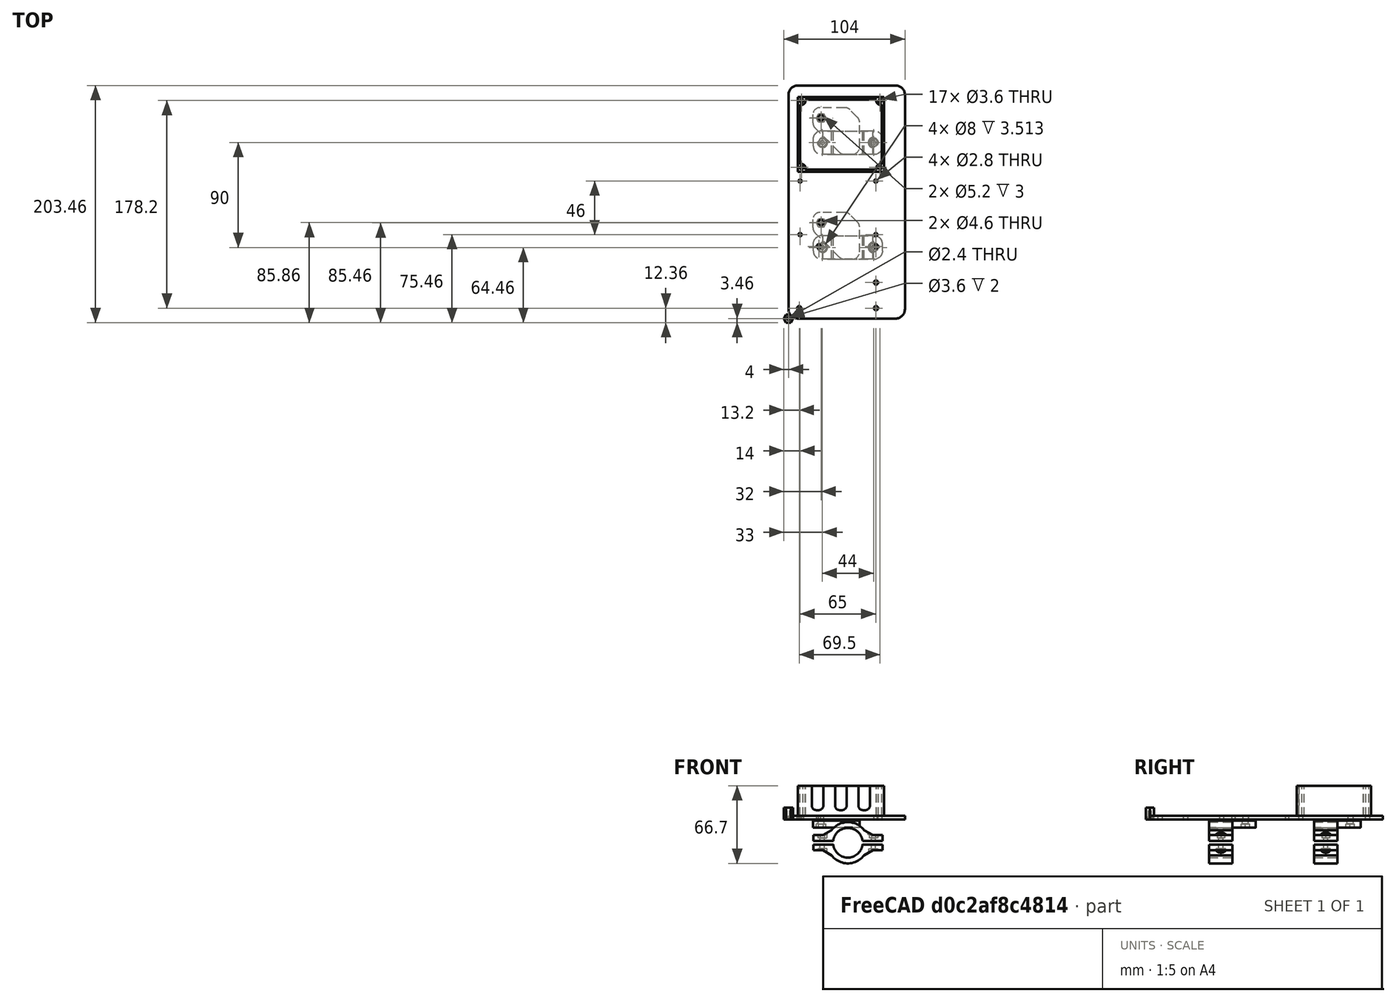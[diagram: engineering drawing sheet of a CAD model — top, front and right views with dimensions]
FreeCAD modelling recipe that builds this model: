
FCSTD DOCUMENT  (FreeCAD 0.18.4R)
Label: cnc_encoders
License: All rights reserved
LicenseURL: http://en.wikipedia.org/wiki/All_rights_reserved
objects: Part::Cylinder×9, PartDesign::FeatureBase×8, PartDesign::Body×8, Part::Cut×7, Part::Box×5, Part::FeaturePython×5, App::Part×3, Part::MultiFuse×2, Part::Fillet×2, Part::Feature×1, Spreadsheet::Sheet×1, Part::Compound×1, Part::RegularPolygon×1, Part::Extrusion×1
note: 50 computed .brp shape members not serialized (recipe doc carries the construction recipe); baked Part::Feature solids carry a one-line shape summary decoded from their .brp

FEATURE [Part::Box] Box  label="base plate"
  AttacherType = Attacher::AttachEngine3D
  Height = 3
  Length = 100
  Width = 200
FEATURE [Part::Cylinder] Cylinder  label="m3 bolt hole"
  Angle = 360
  AttacherType = Attacher::AttachEngine3D
  Height = 10
  Radius = 1.8
FEATURE [PartDesign::FeatureBase] Clone
  BaseFeature = -> Cylinder
FEATURE [PartDesign::Body] Body  label="m3 bolt hole clone"
  BaseFeature = -> Cylinder
  Group = -> [Clone]
  Origin = -> Origin001
  Placement = pos=(-19,27.5,0) rot=(0,0,1;0rad)
  Tip = -> Clone
FEATURE [PartDesign::FeatureBase] Clone001
  BaseFeature = -> Cylinder
FEATURE [PartDesign::Body] Body001  label="m3 bolt hole clone001"
  BaseFeature = -> Cylinder
  Group = -> [Clone001]
  Origin = -> Origin002
  Placement = pos=(-35.8,-25.5,0) rot=(0,0,1;0rad)
  Tip = -> Clone001
FEATURE [PartDesign::FeatureBase] Clone002
  BaseFeature = -> Cylinder
FEATURE [PartDesign::Body] Body002  label="m3 bolt hole clone002"
  BaseFeature = -> Cylinder
  Group = -> [Clone002]
  Origin = -> Origin003
  Placement = pos=(30.2,27.5,0) rot=(0,0,1;0rad)
  Tip = -> Clone002
FEATURE [PartDesign::FeatureBase] Clone003
  BaseFeature = -> Cylinder
FEATURE [PartDesign::Body] Body003  label="m3 bolt hole clone003"
  BaseFeature = -> Cylinder
  Group = -> [Clone003]
  Origin = -> Origin004
  Placement = pos=(30.2,-3.5,0) rot=(0,0,1;0rad)
  Tip = -> Clone003
FEATURE [Part::Feature] cnc_shield_v4_base001
  shape: bbox 75 x 62 x 8 mm, 926 faces, 0 solids (baked)
FEATURE [Part::Box] Box001  label="Cube001"
  AttacherType = Attacher::AttachEngine3D
  Height = 10
  Length = 100
  Placement = pos=(-53,-42,-7) rot=(0,0,1;0rad)
  Width = 100
FEATURE [Part::Cut] Cut  label="test cncv4"
  Base = -> cnc_shield_v4_base001
  Tool = -> Box001
FEATURE [PartDesign::FeatureBase] Clone004
  BaseFeature = -> Cylinder
FEATURE [PartDesign::Body] Body004  label="m3 bolt hole clone004"
  BaseFeature = -> Cylinder
  Group = -> [Clone004]
  Origin = -> Origin005
  Placement = pos=(30.2,-25.5,0) rot=(0,0,1;0rad)
  Tip = -> Clone004
FEATURE [Part::Cylinder] Cylinder001  label="m2.5 bolt hole"
  Angle = 360
  AttacherType = Attacher::AttachEngine3D
  Height = 10
  Radius = 1.4
FEATURE [PartDesign::FeatureBase] Clone005
  BaseFeature = -> Cylinder001
FEATURE [PartDesign::Body] Body005  label="m2.5 bolt hole clone"
  BaseFeature = -> Cylinder001
  Group = -> [Clone005]
  Origin = -> Origin006
  Tip = -> Clone005
FEATURE [Part::FeaturePython] Array  label="m2.5 bolt hole 7x5 pcb array"  # Draft array (typed FeaturePython)
  Angle = 360
  ArrayType = 0
  Axis = (0,0,1)
  Base = -> Body005
  Center = (0,0,0)
  Fuse = false
  IntervalAxis = (0,0,0)
  IntervalX = (65,0,0)
  IntervalY = (0,46,0)
  IntervalZ = (0,0,1)
  NumberPolar = 1
  NumberX = 2
  NumberY = 2
  NumberZ = 1
  Placement = pos=(-35,37.6,0) rot=(0,0,1;0rad)
FEATURE [Part::Cylinder] Cylinder002  label="attach bolt"
  Angle = 360
  AttacherType = Attacher::AttachEngine3D
  Height = 20
  Radius = 2.3
FEATURE [Part::FeaturePython] Array001  label="attach m4 bolt array"  # Draft array (typed FeaturePython)
  Angle = 360
  ArrayType = 0
  Axis = (0,0,1)
  Base = -> Cylinder002
  Center = (0,0,0)
  Fuse = false
  IntervalAxis = (0,0,0)
  IntervalX = (1,0,0)
  IntervalY = (0,90,0)
  IntervalZ = (0,0,1)
  NumberPolar = 1
  NumberX = 1
  NumberY = 2
  NumberZ = 1
  Placement = pos=(-17,48,-6) rot=(0,0,1;0rad)
FEATURE [Spreadsheet::Sheet] Spreadsheet  label="p"
  cells = A1=pcb_length; B1(pcb_length)=70; A2=pcb_width; B2(pcb_width)=50; A3=pcb_hole_x_dist; B3(pcb_hole_x_dist)=65.5; A4=pcb_hole_y_dist; B4(pcb_hole_y_dist)=45.5; A5=bottom_plate_height; B5(bottom_plate_height)=3; A6=bottom_plate_length; B6(bottom_plate_length)=74; A7=bottom_plate_width; B7(bottom_plate_width)=64; A8=bottom_plate_pcb_hole_x_offset; B8(bottom_plate_pcb_hole_x_offset)==(p.bottom_plate_length - p.pcb_hole_x_dist) / 2; A9=bottom_plate_pcb_hole_y_offset; B9(bottom_plate_pcb_hole_y_offset)==(p.bottom_plate_width - p.pcb_hole_y_dist) / 2; A10=box_wall; B10(box_wall)=2; A11=box_wall_height; B11(box_wall_height)=26; A12=box_wall_hole_r; B12(box_wall_hole_r)=1.3; A13=button_hole_r; B13(button_hole_r)=2; A14=tft_hole_length; B14(tft_hole_length)=30; A15=tft_hole_width; B15(tft_hole_width)=14; A16=tft_bolt_hole_dist_x; B16(tft_bolt_hole_dist_x)=25; A17=tft_bolt_hole_dist_y; B17(tft_bolt_hole_dist_y)=19; A19=
FEATURE [Part::Box] Box007  label="wall outer box"
  AttacherType = Attacher::AttachEngine3D
  Height = 26
  Length = 74
  Width = 64
  expr: Height = p.box_wall_height
  expr: Width = p.bottom_plate_width
  expr: Length = p.bottom_plate_length
FEATURE [Part::Box] Box008  label="wall inner extraction"
  AttacherType = Attacher::AttachEngine3D
  Height = 26
  Length = 70
  Placement = pos=(2,2,0) rot=(0,0,1;0rad)
  Width = 60
  expr: Height = p.box_wall_height
  expr: Placement.Base.y = p.box_wall
  expr: Placement.Base.x = p.box_wall
  expr: Width = p.bottom_plate_width - 2 * p.box_wall
  expr: Length = p.bottom_plate_length - 2 * p.box_wall
FEATURE [Part::Cut] Cut004  label="wall box cut"
  Base = -> Box007
  Tool = -> Box008
FEATURE [Part::Cylinder] Cylinder006  label="wall box hole body"
  Angle = 360
  AttacherType = Attacher::AttachEngine3D
  Height = 26
  Radius = 3.3
  expr: Radius = p.box_wall_hole_r + p.box_wall
  expr: Height = p.box_wall_height
FEATURE [Part::Cylinder] Cylinder007  label="wall box hole"
  Angle = 360
  AttacherType = Attacher::AttachEngine3D
  Height = 26
  Radius = 1.3
  expr: Radius = p.box_wall_hole_r
  expr: Height = p.box_wall_height
FEATURE [Part::Cut] Cut005  label="wall box hole stand"
  Base = -> Cylinder006
  Placement = pos=(3.3,3.3,0) rot=(0,0,1;0rad)
  Tool = -> Cylinder007
  expr: Placement.Base.y = p.box_wall + p.box_wall_hole_r
  expr: Placement.Base.x = p.box_wall + p.box_wall_hole_r
FEATURE [Part::FeaturePython] Array004  label="wall box hole stand array"  # Draft array (typed FeaturePython)
  Angle = 360
  ArrayType = 0
  Axis = (0,0,1)
  Base = -> Cut005
  Center = (0,0,0)
  Fuse = false
  IntervalAxis = (0,0,0)
  IntervalX = (67.4,0,0)
  IntervalY = (0,57.4,0)
  IntervalZ = (0,0,1)
  NumberPolar = 1
  NumberX = 2
  NumberY = 2
  NumberZ = 1
  expr: IntervalY.y = p.bottom_plate_width - 2 * (p.box_wall + p.box_wall_hole_r)
  expr: IntervalX.x = p.bottom_plate_length - 2 * (p.box_wall + p.box_wall_hole_r)
FEATURE [Part::MultiFuse] Fusion003  label="wall fusion"
  Placement = pos=(0,0,3) rot=(0,0,1;0rad)
  Shapes = -> [Array004,Cut004]
  expr: Placement.Base.z = p.bottom_plate_height
FEATURE [Part::Box] Box010  label="wall fusion wire hole"
  AttacherType = Attacher::AttachEngine3D
  Height = 21
  Length = 10
  Placement = pos=(34.5,-4.5,8) rot=(0,0,1;0rad)
  Width = 10
  expr: Height = p.box_wall_height - 5
FEATURE [Part::Fillet] Fillet001  label="wall hole fillet"
  Base = -> Box010
  Edges = 2 edges r=4: [Edge4,Edge8]
FEATURE [Part::Cylinder] Cylinder011  label="wall box hole through001"
  Angle = 360
  AttacherType = Attacher::AttachEngine3D
  Height = 20
  Placement = pos=(3.3,3.3,0) rot=(0,0,1;0rad)
  Radius = 1.8
  expr: Placement.Base.y = p.box_wall + p.box_wall_hole_r
  expr: Placement.Base.x = p.box_wall + p.box_wall_hole_r
FEATURE [Part::FeaturePython] Array007  label="wall box hole stand array002"  # Draft array (typed FeaturePython)
  Angle = 360
  ArrayType = 0
  Axis = (0,0,1)
  Base = -> Cylinder011
  Center = (0,0,0)
  Fuse = false
  IntervalAxis = (0,0,0)
  IntervalX = (67.4,0,0)
  IntervalY = (0,57.4,0)
  IntervalZ = (0,0,1)
  NumberPolar = 1
  NumberX = 2
  NumberY = 2
  NumberZ = 1
  Placement = pos=(-37,92,-6) rot=(0,0,1;0rad)
  expr: IntervalY.y = p.bottom_plate_width - 2 * (p.box_wall + p.box_wall_hole_r)
  expr: IntervalX.x = p.bottom_plate_length - 2 * (p.box_wall + p.box_wall_hole_r)
FEATURE [Part::MultiFuse] Fusion  label="cnc v4 m3 hole fusion"
  Placement = pos=(45,34.4,-2.25) rot=(0,0,1;0rad)
  Shapes = -> [Body004,Body003,Body002,Body001,Body,Array001,Array,Array007]
FEATURE [PartDesign::FeatureBase] Clone048
FEATURE [PartDesign::Body] Body050  label="attach part clone002"
  Group = -> [Clone048]
  Origin = -> Origin075
  Tip = -> Clone048
FEATURE [PartDesign::FeatureBase] Clone049
FEATURE [PartDesign::Body] Body051  label="attach part clone003"
  Group = -> [Clone049]
  Origin = -> Origin076
  Placement = pos=(0,0,90) rot=(0,0,1;0rad)
  Tip = -> Clone049
FEATURE [Part::Compound] Compound001  label="attach part compound"
  Links = -> [Body050,Body051]
  Placement = pos=(51,51,-20) rot=(0,0.707107,0.707107;3.14159rad)
FEATURE [Part::Fillet] Fillet  label="base plate fillet"
  Base = -> Box
  Edges = 4 edges r=8: [Edge1,Edge3,Edge5,Edge7]
FEATURE [Part::Cut] Cut008  label="cnc v4 plate cut"
  Base = -> Fillet
  Tool = -> Fusion
FEATURE [App::Part] Part  label="cnc4 encoder pcb plate"
  Group = -> [Box,Cylinder,Box001,cnc_shield_v4_base001,Cut,Body002,Body003,Body001,Body004,Body,Fusion,Cylinder001,Body005,Array,Cylinder002,Array007,Array001,Cylinder011,Cut008]
  Origin = -> Origin
FEATURE [Part::Cylinder] Cylinder012  label="Cylinder"
  Angle = 360
  AttacherType = Attacher::AttachEngine3D
  Height = 7
  Radius = 1.8
FEATURE [Part::Cylinder] Cylinder013  label="Cylinder001"
  Angle = 360
  AttacherType = Attacher::AttachEngine3D
  Height = 2
  Radius = 2.3
FEATURE [Part::Cut] Cut009  label="m2 stand cut"
  Base = -> Cylinder013
  Tool = -> Cylinder012
FEATURE [App::Part] Part001  label="m2 stand"
  Group = -> [Cylinder012,Cylinder013,Cut009]
  Origin = -> Origin077
FEATURE [Part::Cylinder] Cylinder015  label="Cylinder003"
  Angle = 360
  AttacherType = Attacher::AttachEngine3D
  Height = 10
  Radius = 1.2
FEATURE [Part::RegularPolygon] RegularPolygon  label="Regular polygon"
  AttacherType = Attacher::AttachEngine3D
  Circumradius = 4
  Polygon = 6
FEATURE [Part::Extrusion] Extrude
  Base = -> RegularPolygon
  Dir = (0,0,1)
  DirMode = 2
  FaceMakerClass = Part::FaceMakerBullseye
  LengthFwd = 10
  LengthRev = 0
  Solid = true
  Symmetric = false
FEATURE [Part::Cut] Cut010  label="screw hole stand cut"
  Base = -> Extrude
  Tool = -> Cylinder015
FEATURE [App::Part] Part002  label="screw hole stand part"
  Group = -> [Cylinder015,Cut010]
  Origin = -> Origin078
FEATURE [Part::FeaturePython] Array008  label="wall hole array"  # Draft array (typed FeaturePython)
  Angle = 360
  ArrayType = 0
  Axis = (0,0,1)
  Base = -> Fillet001
  Center = (0,0,0)
  Fuse = false
  IntervalAxis = (0,0,0)
  IntervalX = (20,0,0)
  IntervalY = (0,1,0)
  IntervalZ = (0,0,1)
  NumberPolar = 1
  NumberX = 3
  NumberY = 1
  NumberZ = 1
  Placement = pos=(-22.5,0,0) rot=(0,0,1;0rad)
FEATURE [Part::Cut] Cut007  label="wall fusion cut"
  Base = -> Fusion003
  Placement = pos=(8,126,0) rot=(0,0,1;0rad)
  Tool = -> Array008
